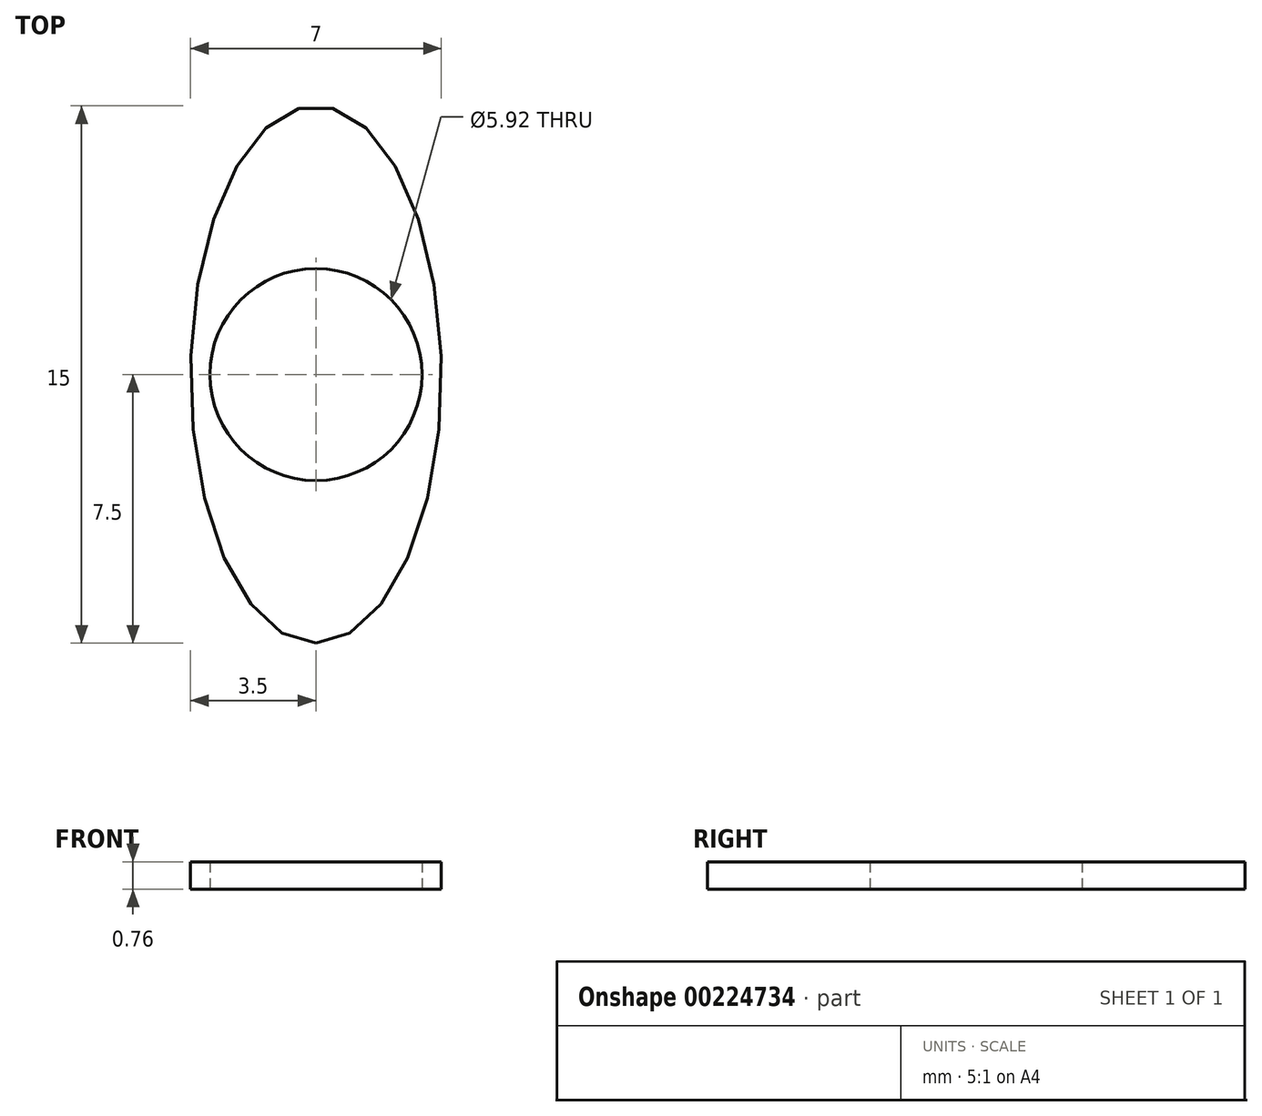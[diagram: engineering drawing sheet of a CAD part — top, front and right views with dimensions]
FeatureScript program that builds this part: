
annotation { "Feature Type Name" : "Feature", "Feature Type Description" : "" }
export const myFeature = defineFeature(function(context is Context, id is Id, definition is map)
    precondition{}
    {
        {
            var Q0;
            Q0=qCreatedBy(makeId("Top.planeOp"),FACE);
            var sketch = newSketch(context, id + "F0", { "sketchPlane" : qUnion([Q0])});
            skCircle(sketch, "E0", {"center": v(0, 0) * mm, "radius": 2.96 * mm});
            skEllipse(sketch, "E1", {"center": v(0, 0) * mm, "majorRadius": 7.5 * mm, "minorRadius": 3.5 * mm, "majorAxis": v(0, -1)});
            skSolve(sketch);
        }
        {
            var Q0;
            Q0 = qSketchRegion(id + "F0", true);
            extrude(context, id + "F1", {"entities" : qUnion([Q0]), "endBound" : BoundingType.SYMMETRIC, "depth" : 0.76 * mm});
        }
    });
